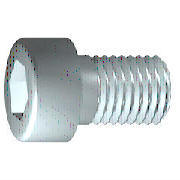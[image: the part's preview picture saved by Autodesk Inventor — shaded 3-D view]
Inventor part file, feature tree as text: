
AUTODESK INVENTOR PART (.ipt)
format: ipt  version: 2022 (Build 260153000, 153)  size: 196,096 bytes
history: native  units: mm (DEFAULTED — no unit token found)
features: sketch x2, extrude x1, plane x1, fillet x1
ambient origin geometry x7: Origin, YZ Plane, XY Plane, X Axis, Y Axis, Z Axis, Center Point
bodies: Solid1 (feature_tree), Body (feature_tree)
feature tree (5):
  extrude  "Slot"  Depth=3.0mm
  plane  "Work Plane1"
  fillet  "Fillet2"  Radius=3.0mm
  sketch  "Sketch1"  dims[d1=6.75mm d2=0.306825mm d3=3.0mm]
  sketch  "Sketch2"  dims[d4=1.3mm d5=60.0deg d6=3.0mm d7=3.0mm d8=2.886751mm d9=5.5mm d10=90.0deg d11=10.0mm d12=0.0mm d13=6.75mm d14=0.0mm d15=0.306725mm d16=0.306725mm d17=0.3mm d19=0.0mm d26=8.0mm d27=45.0deg d28=0.0mm d29=0.0mm d30=0.1mm]
